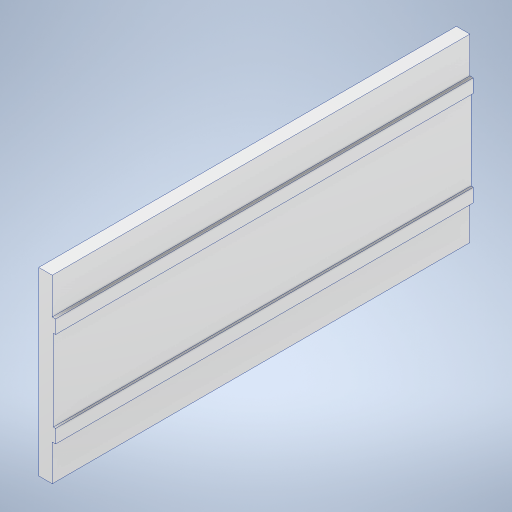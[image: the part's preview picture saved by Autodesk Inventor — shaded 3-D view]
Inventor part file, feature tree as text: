
AUTODESK INVENTOR PART (.ipt)
format: ipt  version: 2024 (Build 280153000, 153)  size: 313,856 bytes
history: native  units: mm
features: extrude x7, sketch x7, projected_geometry x3
ambient origin geometry x8: Origin, YZ Plane, XZ Plane, XY Plane, X Axis, Y Axis, Z Axis, Center Point
bodies: Solid1 (feature_tree)
feature tree (17):
  extrude  "Extrusion1"  Depth=160.0mm TaperAngle=0.0deg
  extrude  "Extrusion2"  Depth=25.0mm
  extrude  "Extrusion3"  Depth=45.0mm
  extrude  "Extrusion4"  Depth=4.0mm
  extrude  "Extrusion5"  Depth=80.0mm
  extrude  "Extrusion6"  Depth=150.0mm TaperAngle=0.0deg
  extrude  "Extrusion7"  Depth=370.0mm
  sketch  "Sketch1"  dims[d0=475.0mm d1=160.0mm d2=0.0mm]
  sketch  "Sketch2"  dims[d4=25.0mm d5=25.0mm]
  sketch  "Sketch3"  dims[d6=10.0mm d7=45.0mm]
  sketch  "Sketch4"  dims[d8=45.0mm d9=4.0mm]
  projected_geometry  "Projected Loop1"
  projected_geometry  "Projected Loop2"
  sketch  "Sketch5"  dims[d10=36.0mm d11=80.0mm]
  projected_geometry  "Projected Loop3"
  sketch  "Sketch6"  dims[d12=80.0mm d13=150.0mm d14=0.0mm]
  sketch  "Sketch7"  dims[d15=20.0mm d16=370.0mm d17=200.0mm d18=0.0mm d19=30.0mm d20=0.0mm d21=5.0mm d22=0.0mm d23=13.0mm d24=13.0mm d25=3.0mm d26=500.0mm d27=0.0mm d28=1.0mm d29=1.0mm d30=2.0mm d31=1000.0mm d32=0.0mm]
